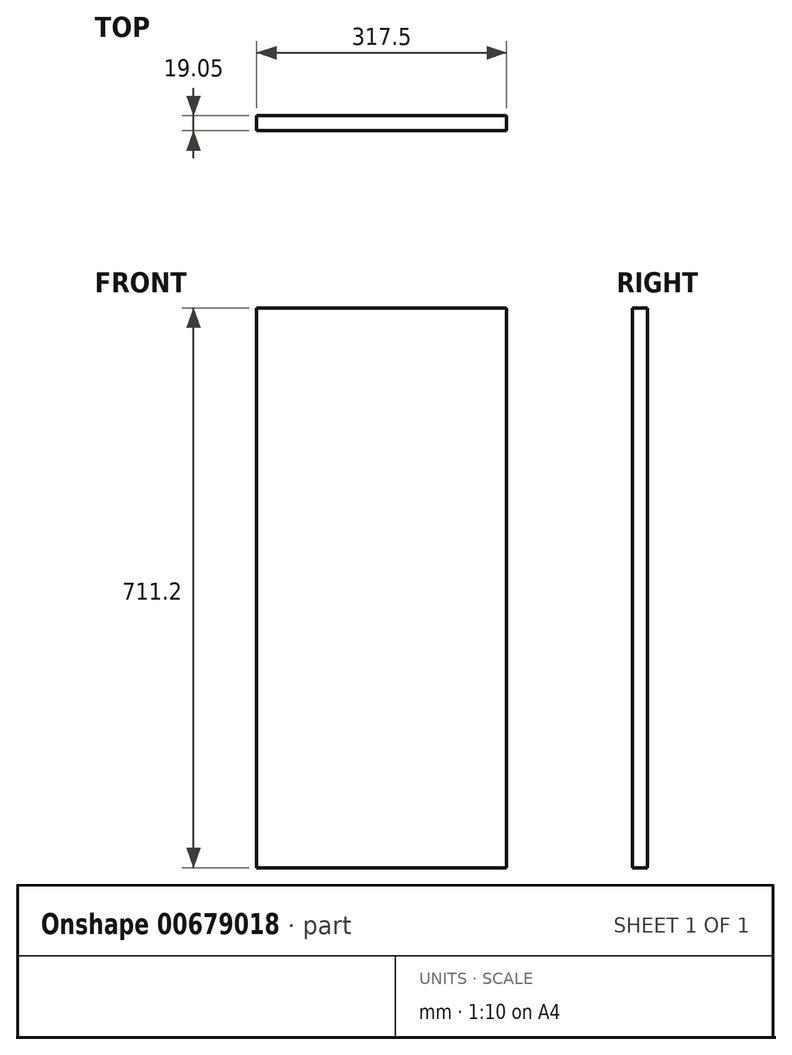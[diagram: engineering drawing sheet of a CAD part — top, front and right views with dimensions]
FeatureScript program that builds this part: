
annotation { "Feature Type Name" : "Feature", "Feature Type Description" : "" }
export const myFeature = defineFeature(function(context is Context, id is Id, definition is map)
    precondition{}
    {
        {
            var Q0;
            Q0=qCreatedBy(makeId("Front.planeOp"),FACE);
            var sketch = newSketch(context, id + "F0", { "sketchPlane" : qUnion([Q0])});
            skLineSegment(sketch, "E0.bottom", {"start": v(-158.75, 355.6) * mm, "end": v(158.75, 355.6) * mm});
            skLineSegment(sketch, "E0.top", {"start": v(-158.75, -355.6) * mm, "end": v(158.75, -355.6) * mm});
            skLineSegment(sketch, "E0.left", {"start": v(-158.75, 355.6) * mm, "end": v(-158.75, -355.6) * mm});
            skLineSegment(sketch, "E0.right", {"start": v(158.75, 355.6) * mm, "end": v(158.75, -355.6) * mm});
            skPoint(sketch, "E0.middle", {"position": v(0, 0) * mm});
            skSolve(sketch);
        }
        {
            var Q0;
            Q0=makeQuery(id+"F0.imprint","IMPRINT",FACE,{"disambiguationData":[TD([[makeQuery(id+"F0.imprint","IMPRINT",EDGE,{"derivedFrom":sQuery(id+"F0.wireOp",EDGE,"E0.bottom")}),-1.0]])]});
            extrude(context, id + "F1", {"entities" : qUnion([Q0]), "depth" : 19.05 * mm, "offsetDistance" : 25.4 * mm});
        }
    });
